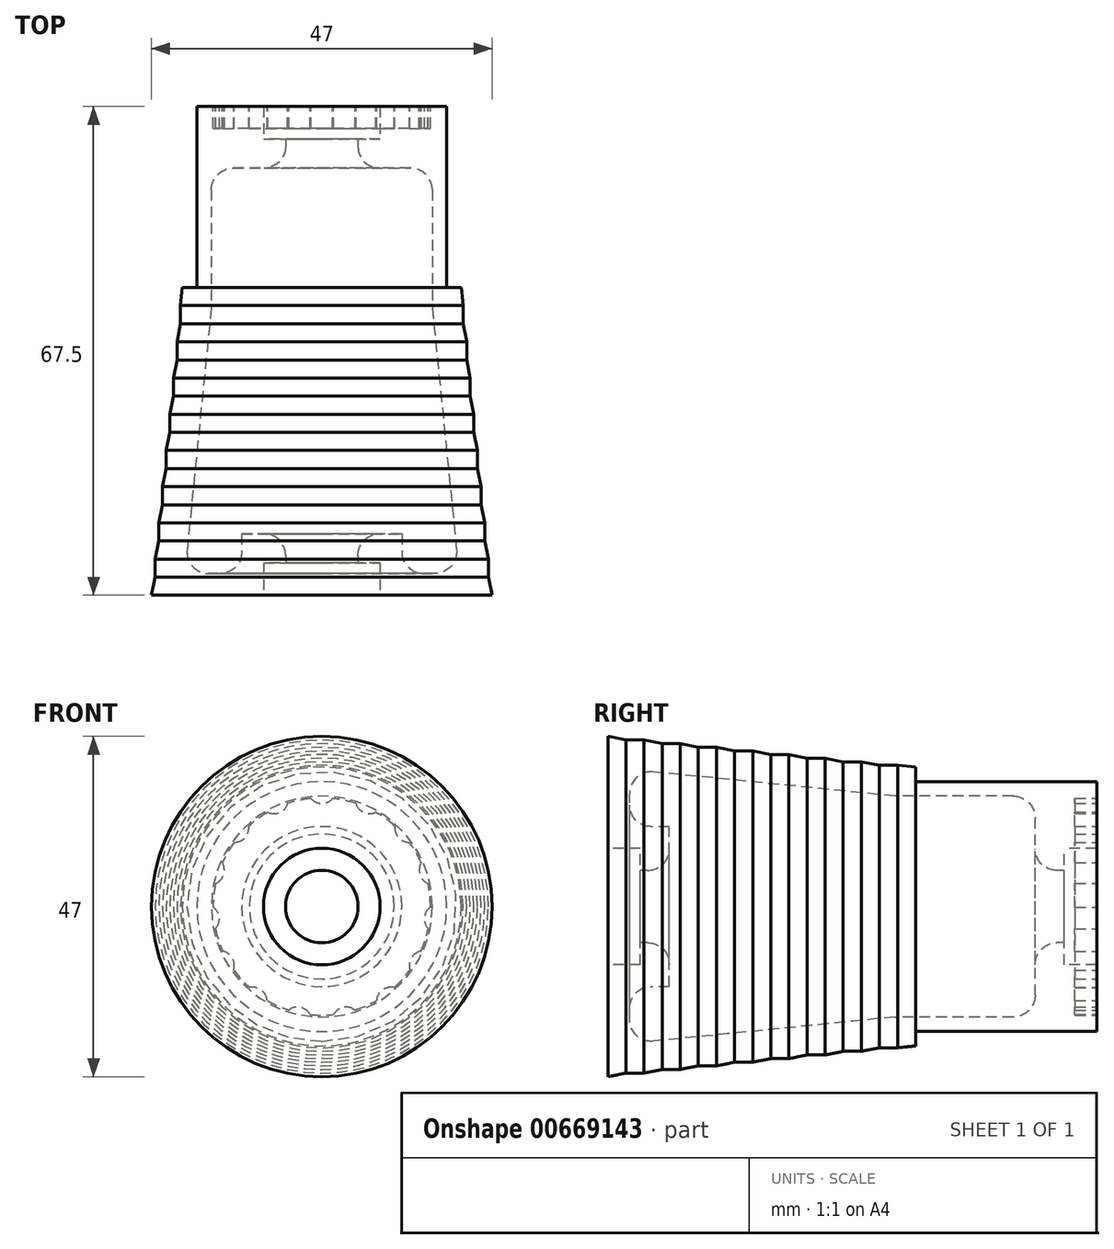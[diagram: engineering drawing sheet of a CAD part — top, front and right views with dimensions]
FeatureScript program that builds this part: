
annotation { "Feature Type Name" : "Feature", "Feature Type Description" : "" }
export const myFeature = defineFeature(function(context is Context, id is Id, definition is map)
    precondition{}
    {
        {
            var Q0;
            Q0=qCreatedBy(makeId("Right.planeOp"),FACE);
            var sketch = newSketch(context, id + "F0", { "sketchPlane" : qUnion([Q0])});
            skLineSegment(sketch, "E0", {"start": v(0, 5) * mm, "end": v(0, 8.05) * mm});
            skLineSegment(sketch, "E1", {"start": v(0, 8.05) * mm, "end": v(-4.5, 8.05) * mm});
            skLineSegment(sketch, "E2", {"start": v(-4.5, 8.05) * mm, "end": v(-4.5, 23.5) * mm});
            skLineSegment(sketch, "E3", {"start": v(-4.5, 23.5) * mm, "end": v(-2, 23) * mm});
            skLineSegment(sketch, "E4", {"start": v(-2, 23) * mm, "end": v(0.5, 23) * mm});
            skLineSegment(sketch, "E5", {"start": v(0.5, 23) * mm, "end": v(3, 22.5) * mm});
            skLineSegment(sketch, "E6", {"start": v(3, 22.5) * mm, "end": v(5.5, 22.5) * mm});
            skLineSegment(sketch, "E7", {"start": v(5.5, 22.5) * mm, "end": v(8, 22) * mm});
            skLineSegment(sketch, "E8", {"start": v(8, 22) * mm, "end": v(10.5, 22) * mm});
            skLineSegment(sketch, "E9", {"start": v(10.5, 22) * mm, "end": v(13, 21.5) * mm});
            skLineSegment(sketch, "E10", {"start": v(13, 21.5) * mm, "end": v(15.5, 21.5) * mm});
            skLineSegment(sketch, "E11", {"start": v(15.5, 21.5) * mm, "end": v(18, 21) * mm});
            skLineSegment(sketch, "E12", {"start": v(18, 21) * mm, "end": v(20.5, 21) * mm});
            skLineSegment(sketch, "E13", {"start": v(20.5, 21) * mm, "end": v(23, 20.5) * mm});
            skLineSegment(sketch, "E14", {"start": v(23, 20.5) * mm, "end": v(25.5, 20.5) * mm});
            skLineSegment(sketch, "E15", {"start": v(25.5, 20.5) * mm, "end": v(28, 20) * mm});
            skLineSegment(sketch, "E16", {"start": v(28, 20) * mm, "end": v(30.5, 20) * mm});
            skLineSegment(sketch, "E17", {"start": v(30.5, 20) * mm, "end": v(33, 19.5) * mm});
            skLineSegment(sketch, "E18", {"start": v(33, 19.5) * mm, "end": v(35.5, 19.5) * mm});
            skLineSegment(sketch, "E19", {"start": v(38, 19.25) * mm, "end": v(38, 17.25) * mm});
            skLineSegment(sketch, "E20", {"start": v(38, 17.25) * mm, "end": v(63, 17.25) * mm});
            skLineSegment(sketch, "E21", {"start": v(0, 0) * mm, "end": v(49.8, 0) * mm, "construction": true});
            skLineSegment(sketch, "E22", {"start": v(0, 5) * mm, "end": v(1, 5) * mm});
            skLineSegment(sketch, "E23", {"start": v(4, 8) * mm, "end": v(4, 11.05) * mm});
            skLineSegment(sketch, "E24", {"start": v(35.45, 15.25) * mm, "end": v(51.5, 15.25) * mm});
            skLineSegment(sketch, "E25", {"start": v(35.5, 19.5) * mm, "end": v(38, 19.25) * mm});
            skLineSegment(sketch, "E26", {"start": v(35.15, 15.26) * mm, "end": v(1.8, 18.6) * mm});
            skLineSegment(sketch, "E27", {"start": v(-1.5, 15.62) * mm, "end": v(-1.5, 14.05) * mm});
            skLineSegment(sketch, "E28", {"start": v(1.5, 11.05) * mm, "end": v(4, 11.05) * mm});
            skPoint(sketch, "E29.visualSharp", {"position": v(-1.5, 18.93) * mm});
            skArc(sketch, "E29.filletArc", {"start": v(1.8, 18.6) * mm, "mid": v(-0.51, 17.84) * mm, "end": v(-1.5, 15.62) * mm});
            skPoint(sketch, "E30.visualSharp", {"position": v(-1.5, 11.05) * mm});
            skArc(sketch, "E30.filletArc", {"start": v(-1.5, 14.05) * mm, "mid": v(-0.62, 11.93) * mm, "end": v(1.5, 11.05) * mm});
            skLineSegment(sketch, "E31", {"start": v(54.5, 12.25) * mm, "end": v(54.5, 8) * mm});
            skLineSegment(sketch, "E32", {"start": v(57.5, 5) * mm, "end": v(58.5, 5) * mm});
            skLineSegment(sketch, "E33", {"start": v(58.5, 5) * mm, "end": v(58.5, 8.05) * mm});
            skLineSegment(sketch, "E34", {"start": v(58.5, 8.05) * mm, "end": v(63, 8.05) * mm});
            skLineSegment(sketch, "E35", {"start": v(63, 8.05) * mm, "end": v(63, 17.25) * mm});
            skPoint(sketch, "E36.visualSharp", {"position": v(54.5, 15.25) * mm});
            skArc(sketch, "E36.filletArc", {"start": v(54.5, 12.25) * mm, "mid": v(53.62, 14.37) * mm, "end": v(51.5, 15.25) * mm});
            skPoint(sketch, "E37.visualSharp", {"position": v(35.3, 15.25) * mm});
            skArc(sketch, "E37.filletArc", {"start": v(35.15, 15.26) * mm, "mid": v(35.3, 15.25) * mm, "end": v(35.45, 15.25) * mm});
            skPoint(sketch, "E38.visualSharp", {"position": v(54.5, 5) * mm});
            skArc(sketch, "E38.filletArc", {"start": v(54.5, 8) * mm, "mid": v(55.38, 5.88) * mm, "end": v(57.5, 5) * mm});
            skPoint(sketch, "E39.visualSharp", {"position": v(4, 5) * mm});
            skArc(sketch, "E39.filletArc", {"start": v(1, 5) * mm, "mid": v(3.12, 5.88) * mm, "end": v(4, 8) * mm});
            skSolve(sketch);
        }
        {
            var Q0;
            Q0=makeQuery(id+"F0.imprint","IMPRINT",FACE,{"disambiguationData":[TD([[makeQuery(id+"F0.imprint","IMPRINT",EDGE,{"derivedFrom":sQuery(id+"F0.wireOp",EDGE,"E0")}),-1.0]])]});
            var Q1;
            Q1=sQuery(id+"F0.wireOp",EDGE,"E21");
            revolve(context, id + "F1", {"entities" : qUnion([Q0]), "axis" : qUnion([Q1]), "revolveType" : RevolveType.FULL});
        }
        {
            var Q0;
            Q0=makeQuery(id+"F1.opRevolve","SWEPT_FACE",FACE,{"disambiguationData":[OSD([sQuery(id+"F0.wireOp",EDGE,"E35")])]});
            var sketch = newSketch(context, id + "F2", { "sketchPlane" : qUnion([Q0])});
            skCircle(sketch, "E40", {"center": v(0, 0) * mm, "radius": 10 * mm});
            skArc(sketch, "E41", {"start": v(-1.5, 14.92) * mm, "mid": v(0, 14.25) * mm, "end": v(1.5, 14.92) * mm});
            skArc(sketch, "E42.1.0", {"start": v(-7.44, 13.02) * mm, "mid": v(-5.8, 13.02) * mm, "end": v(-4.7, 14.24) * mm});
            skArc(sketch, "E42.2.0", {"start": v(-12.1, 8.87) * mm, "mid": v(-10.59, 9.53) * mm, "end": v(-10.09, 11.1) * mm});
            skArc(sketch, "E42.3.0", {"start": v(-14.66, 3.19) * mm, "mid": v(-13.55, 4.4) * mm, "end": v(-13.73, 6.04) * mm});
            skArc(sketch, "E42.4.0", {"start": v(-14.69, -3.05) * mm, "mid": v(-14.17, -1.49) * mm, "end": v(-15, -0.07) * mm});
            skArc(sketch, "E42.5.0", {"start": v(-12.18, -8.76) * mm, "mid": v(-12.34, -7.12) * mm, "end": v(-13.68, -6.16) * mm});
            skArc(sketch, "E42.6.0", {"start": v(-7.56, -12.96) * mm, "mid": v(-8.37, -11.53) * mm, "end": v(-9.99, -11.2) * mm});
            skArc(sketch, "E42.7.0", {"start": v(-1.64, -14.91) * mm, "mid": v(-2.96, -13.94) * mm, "end": v(-4.57, -14.29) * mm});
            skArc(sketch, "E42.8.0", {"start": v(4.57, -14.29) * mm, "mid": v(2.96, -13.94) * mm, "end": v(1.64, -14.91) * mm});
            skArc(sketch, "E42.9.0", {"start": v(9.99, -11.2) * mm, "mid": v(8.37, -11.53) * mm, "end": v(7.56, -12.96) * mm});
            skArc(sketch, "E42.10.0", {"start": v(13.68, -6.16) * mm, "mid": v(12.34, -7.12) * mm, "end": v(12.18, -8.76) * mm});
            skArc(sketch, "E42.11.0", {"start": v(15, -0.07) * mm, "mid": v(14.17, -1.49) * mm, "end": v(14.69, -3.05) * mm});
            skArc(sketch, "E42.12.0", {"start": v(13.73, 6.04) * mm, "mid": v(13.55, 4.4) * mm, "end": v(14.66, 3.19) * mm});
            skArc(sketch, "E42.13.0", {"start": v(10.09, 11.1) * mm, "mid": v(10.59, 9.53) * mm, "end": v(12.1, 8.87) * mm});
            skArc(sketch, "E42.14.0", {"start": v(4.7, 14.24) * mm, "mid": v(5.8, 13.02) * mm, "end": v(7.44, 13.02) * mm});
            skArc(sketch, "E43", {"start": v(4.7, 14.24) * mm, "mid": v(3.12, 14.67) * mm, "end": v(1.5, 14.92) * mm});
            skCircle(sketch, "E44.1.0", {"center": v(0, 0) * mm, "radius": 15 * mm, "construction": true});
            skArc(sketch, "E45.1.1", {"start": v(-1.5, 14.92) * mm, "mid": v(-3.12, 14.67) * mm, "end": v(-4.7, 14.24) * mm});
            skArc(sketch, "E45.2.1", {"start": v(-7.44, 13.02) * mm, "mid": v(-8.82, 12.14) * mm, "end": v(-10.09, 11.1) * mm});
            skArc(sketch, "E45.3.1", {"start": v(-12.1, 8.87) * mm, "mid": v(-13, 7.5) * mm, "end": v(-13.73, 6.04) * mm});
            skArc(sketch, "E45.4.1", {"start": v(-14.66, 3.19) * mm, "mid": v(-14.92, 1.57) * mm, "end": v(-15, -0.07) * mm});
            skArc(sketch, "E45.5.1", {"start": v(-14.69, -3.05) * mm, "mid": v(-14.27, -4.64) * mm, "end": v(-13.68, -6.16) * mm});
            skArc(sketch, "E45.6.1", {"start": v(-12.18, -8.76) * mm, "mid": v(-11.15, -10.04) * mm, "end": v(-9.99, -11.2) * mm});
            skArc(sketch, "E45.7.1", {"start": v(-7.56, -12.96) * mm, "mid": v(-6.1, -13.7) * mm, "end": v(-4.57, -14.29) * mm});
            skArc(sketch, "E45.8.1", {"start": v(-1.64, -14.91) * mm, "mid": v(0, -15) * mm, "end": v(1.64, -14.91) * mm});
            skArc(sketch, "E45.9.1", {"start": v(4.57, -14.29) * mm, "mid": v(6.1, -13.7) * mm, "end": v(7.56, -12.96) * mm});
            skArc(sketch, "E45.10.1", {"start": v(9.99, -11.2) * mm, "mid": v(11.15, -10.04) * mm, "end": v(12.18, -8.76) * mm});
            skArc(sketch, "E45.11.1", {"start": v(13.68, -6.16) * mm, "mid": v(14.27, -4.64) * mm, "end": v(14.69, -3.05) * mm});
            skArc(sketch, "E45.12.1", {"start": v(15, -0.07) * mm, "mid": v(14.92, 1.57) * mm, "end": v(14.66, 3.19) * mm});
            skArc(sketch, "E45.13.1", {"start": v(13.73, 6.04) * mm, "mid": v(13, 7.5) * mm, "end": v(12.1, 8.87) * mm});
            skArc(sketch, "E45.14.1", {"start": v(10.09, 11.1) * mm, "mid": v(8.82, 12.14) * mm, "end": v(7.44, 13.02) * mm});
            skSolve(sketch);
        }
        {
            var Q0;
            Q0 = qSketchRegion(id + "F2", true);
            extrude(context, id + "F3", {"entities" : qUnion([Q0]), "operationType" : NewBodyOperationType.REMOVE, "oppositeDirection" : true, "depth" : 3 * mm, "offsetDistance" : 25 * mm});
        }
    });
